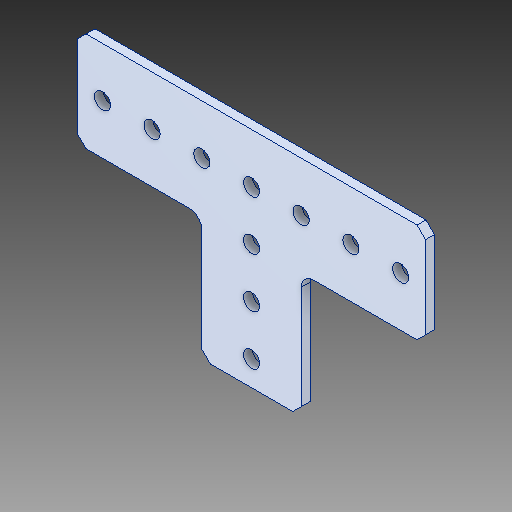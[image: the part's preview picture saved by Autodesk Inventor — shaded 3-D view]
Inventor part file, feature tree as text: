
AUTODESK INVENTOR PART (.ipt)
format: ipt  version: 2018 (Build 220112000, 112)  size: 115,200 bytes
history: native  units: in
note: dims shown in document units (in); Inventor stores cm internally (conversion verified against a paired STEP export)
features: fillet x1
ambient origin geometry x8: Origin, YZ Plane, XZ Plane, XY Plane, X Axis, Y Axis, Z Axis, Center Point
bodies: Solid1 (feature_tree)
feature tree (1):
  fillet  "Fillet1"  [1 undecoded]
note: 1 required parameter value undecoded (feature->parameter linkage not recoverable at this tier; creation-order binding heuristic only, values carry confidence <= 0.55)
